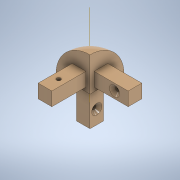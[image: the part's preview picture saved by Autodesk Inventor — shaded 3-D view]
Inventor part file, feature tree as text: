
AUTODESK INVENTOR PART (.ipt)
format: ipt  version: 2022 (Build 260153000, 153)  size: 149,504 bytes
history: native  units: mm
features: other x3, sketch x2, extrude x2, hole x1, pattern_circular x1
ambient origin geometry x8: Origin, YZ Plane, XZ Plane, XY Plane, X Axis, Y Axis, Z Axis, Center Point
bodies: Body1 (feature_tree)
feature tree (9):
  other  "Těleso1"
  sketch  "Náčrt1"
  extrude  "Vysunutí1"  Depth=50.0mm
  other  "Pracovní osa1"
  other  "Rotace1"
  extrude  "Vysunutí2"  Depth=50.0mm
  hole  "Díra1"  [1 undecoded]
  pattern_circular  "Kruhové pole1"  [2 undecoded]
  sketch  "Náčrt2"
note: 3 required parameter values undecoded (feature->parameter linkage not recoverable at this tier; creation-order binding heuristic only, values carry confidence <= 0.55)
